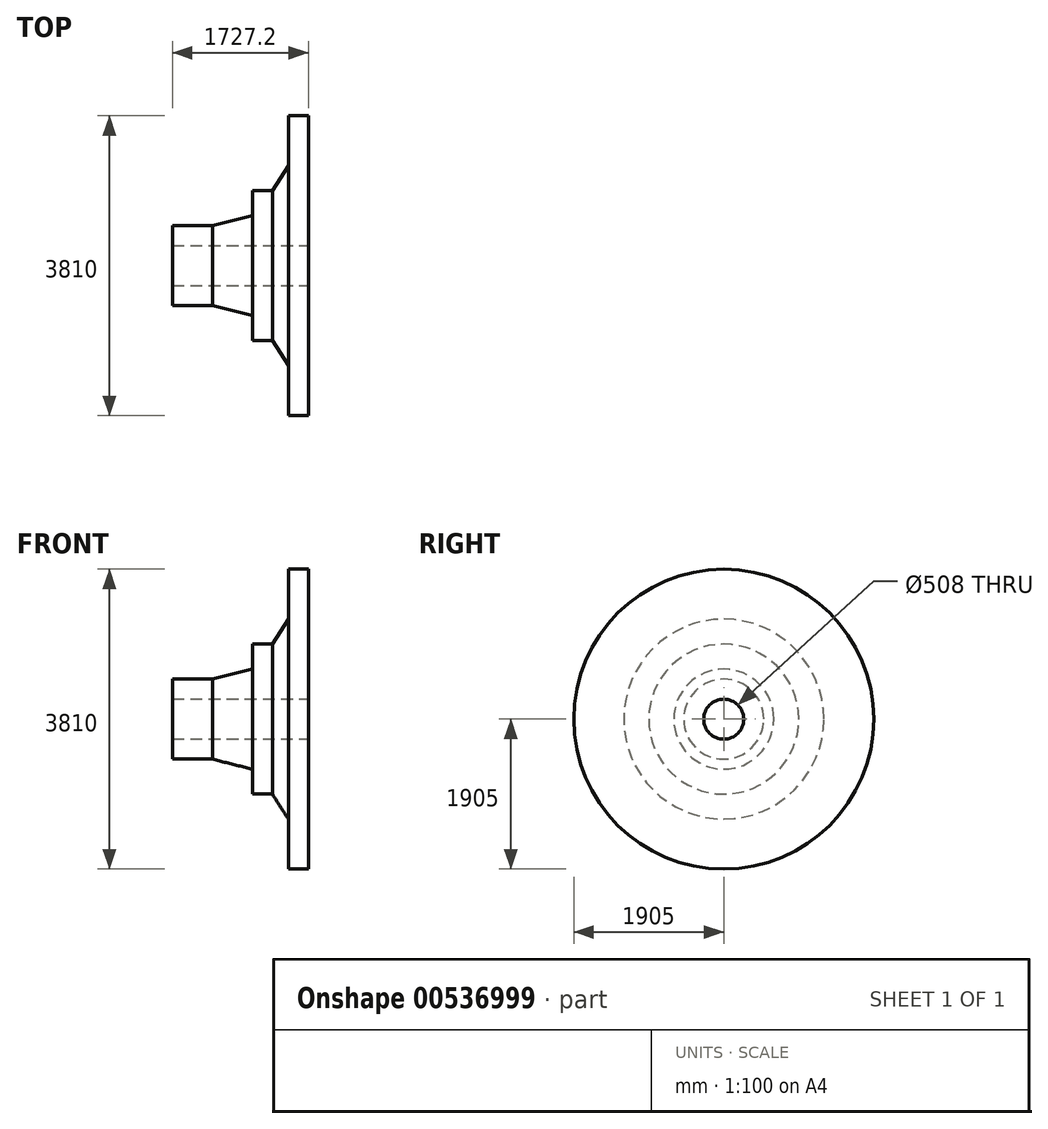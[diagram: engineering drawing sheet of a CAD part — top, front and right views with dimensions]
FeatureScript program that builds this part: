
annotation { "Feature Type Name" : "Feature", "Feature Type Description" : "" }
export const myFeature = defineFeature(function(context is Context, id is Id, definition is map)
    precondition{}
    {
        {
            var Q0;
            Q0=qCreatedBy(makeId("Front.planeOp"),FACE);
            var sketch = newSketch(context, id + "F0", { "sketchPlane" : qUnion([Q0])});
            skLineSegment(sketch, "E0", {"start": v(757.8, 0) * mm, "end": v(-971.72, 0) * mm});
            skLineSegment(sketch, "E1", {"start": v(757.8, 1905) * mm, "end": v(503.8, 1905) * mm});
            skLineSegment(sketch, "E2", {"start": v(757.8, 254) * mm, "end": v(-969.4, 254) * mm});
            skLineSegment(sketch, "E3", {"start": v(-969.4, 254) * mm, "end": v(-969.4, 508) * mm});
            skLineSegment(sketch, "E4", {"start": v(-969.4, 508) * mm, "end": v(-461.4, 508) * mm});
            skLineSegment(sketch, "E5", {"start": v(503.8, 1905) * mm, "end": v(503.8, 1270) * mm});
            skLineSegment(sketch, "E6", {"start": v(503.8, 1270) * mm, "end": v(300.6, 952.5) * mm});
            skLineSegment(sketch, "E7", {"start": v(300.6, 952.5) * mm, "end": v(46.6, 952.5) * mm});
            skLineSegment(sketch, "E8", {"start": v(46.6, 952.5) * mm, "end": v(46.6, 635) * mm});
            skLineSegment(sketch, "E9", {"start": v(46.6, 635) * mm, "end": v(-461.4, 508) * mm});
            skLineSegment(sketch, "E10", {"start": v(757.8, 254) * mm, "end": v(757.8, 1905) * mm});
            skLineSegment(sketch, "E11.MirrorCS", {"start": v(757.8, -254) * mm, "end": v(757.8, -1905) * mm});
            skLineSegment(sketch, "E12.MirrorCS", {"start": v(757.8, -1905) * mm, "end": v(503.8, -1905) * mm});
            skLineSegment(sketch, "E13.MirrorCS", {"start": v(757.8, -254) * mm, "end": v(-969.4, -254) * mm});
            skLineSegment(sketch, "E14.MirrorCS", {"start": v(-969.4, -254) * mm, "end": v(-969.4, -508) * mm});
            skLineSegment(sketch, "E15.MirrorCS", {"start": v(503.8, -1270) * mm, "end": v(300.6, -952.5) * mm});
            skLineSegment(sketch, "E16.MirrorCS", {"start": v(46.6, -635) * mm, "end": v(-461.4, -508) * mm});
            skLineSegment(sketch, "E17.MirrorCS", {"start": v(300.6, -952.5) * mm, "end": v(46.6, -952.5) * mm});
            skLineSegment(sketch, "E18.MirrorCS", {"start": v(503.8, -1905) * mm, "end": v(503.8, -1270) * mm});
            skLineSegment(sketch, "E19.MirrorCS", {"start": v(-969.4, -508) * mm, "end": v(-461.4, -508) * mm});
            skLineSegment(sketch, "E20.MirrorCS", {"start": v(46.6, -952.5) * mm, "end": v(46.6, -635) * mm});
            skSolve(sketch);
        }
        {
            var Q0;
            Q0=makeQuery(id+"F0.imprint","IMPRINT",FACE,{"disambiguationData":[TD([[makeQuery(id+"F0.imprint","IMPRINT",EDGE,{"derivedFrom":sQuery(id+"F0.wireOp",EDGE,"E1")}),1.0]])]});
            var Q1;
            Q1=sQuery(id+"F0.wireOp",EDGE,"E0");
            revolve(context, id + "F1", {"entities" : qUnion([Q0]), "axis" : qUnion([Q1]), "revolveType" : RevolveType.FULL});
        }
    });
